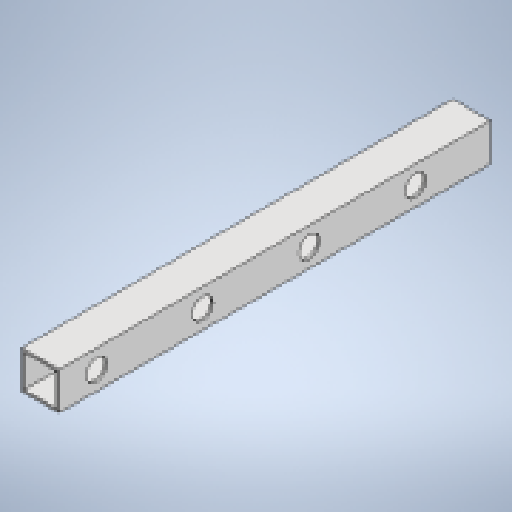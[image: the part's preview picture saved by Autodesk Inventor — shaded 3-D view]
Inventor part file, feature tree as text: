
AUTODESK INVENTOR PART (.ipt)
format: ipt  version: 2025.3 (Build 293356030, 356C)  size: 193,536 bytes
history: native  units: mm
features: extrude x2, sketch x2, pattern_linear x1
ambient origin geometry x8: Origin, YZ Plane, XZ Plane, XY Plane, X Axis, Y Axis, Z Axis, Center Point
bodies: Body1 (feature_tree)
feature tree (5):
  extrude  "Extrusion3"  Depth=30.0mm
  extrude  "Extrusion4"  Depth=2.0mm
  pattern_linear  "Rectangular Pattern4"  Spacing1=345.0mm  [1 undecoded]
  sketch  "Sketch9"  dims[d61=340.0mm d172=30.0mm]
  sketch  "Sketch10"  dims[d173=30.0mm d174=2.0mm d175=345.0mm d176=0.0mm d177=17.0mm d178=17.0mm d179=0.0mm d180=0.0mm d181=30.0mm d182=90.0mm d186=17.0mm d187=40.0mm d189=85.0mm]
note: 1 required parameter value undecoded (feature->parameter linkage not recoverable at this tier; creation-order binding heuristic only, values carry confidence <= 0.55)
